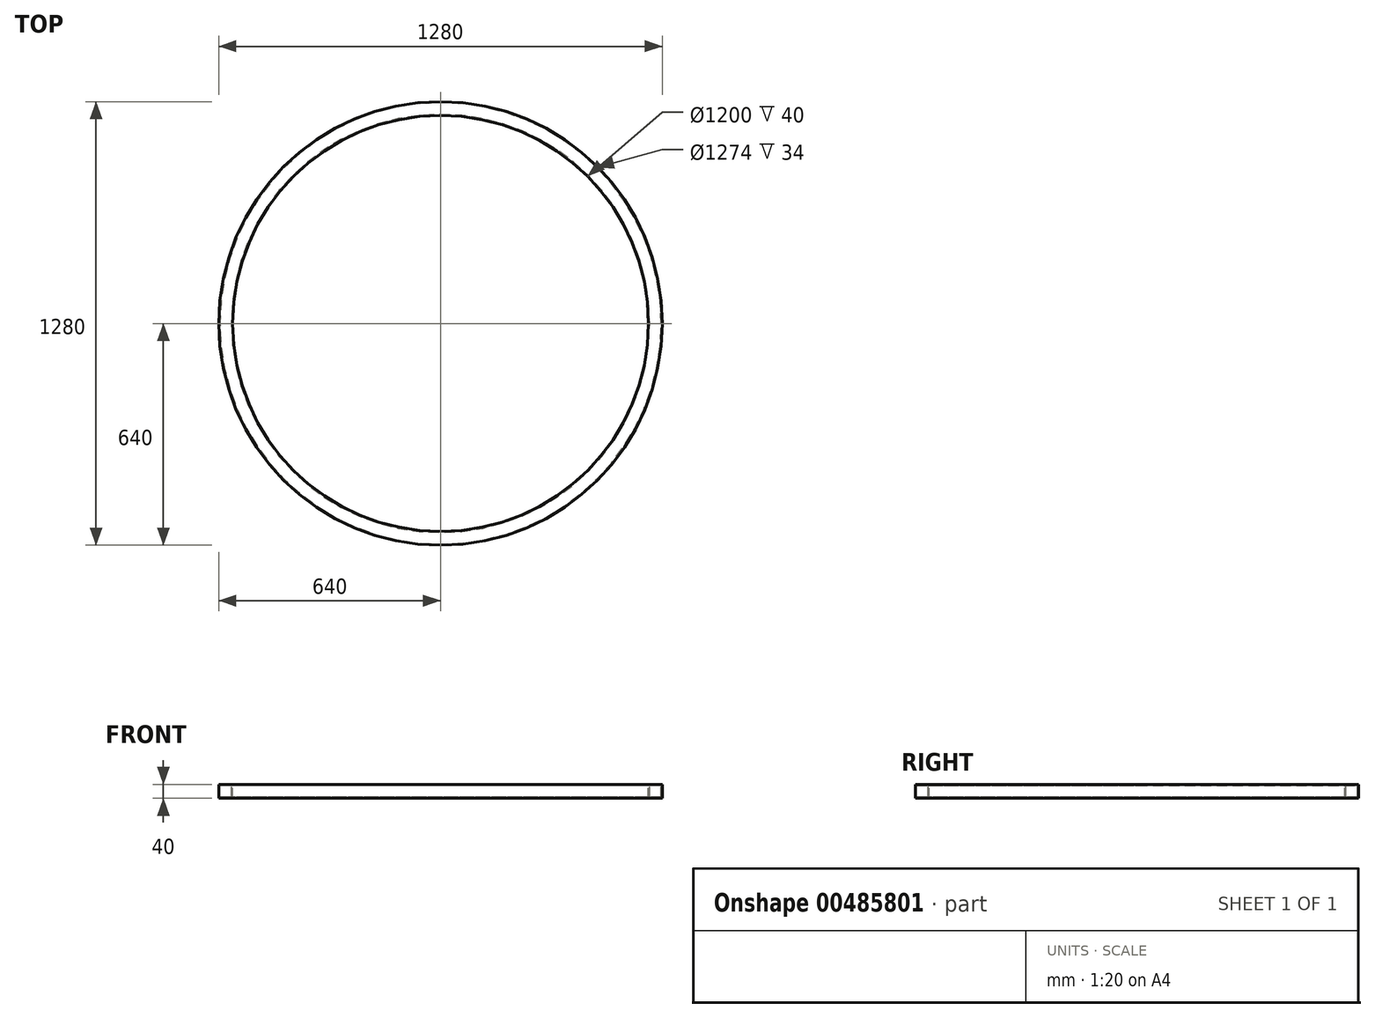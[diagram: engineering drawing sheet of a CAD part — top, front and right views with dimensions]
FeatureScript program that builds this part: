
annotation { "Feature Type Name" : "Feature", "Feature Type Description" : "" }
export const myFeature = defineFeature(function(context is Context, id is Id, definition is map)
    precondition{}
    {
        {
            var Q0;
            Q0=qCreatedBy(makeId("Front.planeOp"),FACE);
            var sketch = newSketch(context, id + "F0", { "sketchPlane" : qUnion([Q0])});
            skLineSegment(sketch, "E0.bottom", {"start": v(-640, 20) * mm, "end": v(-600, 20) * mm});
            skLineSegment(sketch, "E0.top", {"start": v(-640, -20) * mm, "end": v(-600, -20) * mm});
            skLineSegment(sketch, "E0.left", {"start": v(-640, 20) * mm, "end": v(-640, -20) * mm});
            skLineSegment(sketch, "E0.right", {"start": v(-600, 20) * mm, "end": v(-600, -20) * mm});
            skLineSegment(sketch, "E1", {"start": v(0, 102.9) * mm, "end": v(0, -178.06) * mm, "construction": true});
            skLineSegment(sketch, "E2.0", {"start": v(-637, 17) * mm, "end": v(-603, 17) * mm});
            skLineSegment(sketch, "E2.1", {"start": v(-637, 17) * mm, "end": v(-637, -17) * mm});
            skLineSegment(sketch, "E2.2", {"start": v(-637, -17) * mm, "end": v(-603, -17) * mm});
            skLineSegment(sketch, "E2.3", {"start": v(-603, 17) * mm, "end": v(-603, -17) * mm});
            skSolve(sketch);
        }
        {
            var Q0;
            Q0 = qSketchRegion(id + "F0", true);
            var Q1;
            Q1=sQuery(id+"F0.wireOp",EDGE,"E1");
            revolve(context, id + "F1", {"entities" : qUnion([Q0]), "axis" : qUnion([Q1]), "revolveType" : RevolveType.FULL});
        }
        {
            var Q0;
            Q0=qCreatedBy(makeId("Front.planeOp"),FACE);
            cPlane(context, id + "F2", {"entities" : qUnion([Q0]), "cplaneType" : CPlaneType.OFFSET, "offset" : ((1200 + 20 + 20) / 2) * mm, "width" : 150 * mm, "height" : 150 * mm});
        }
    });
